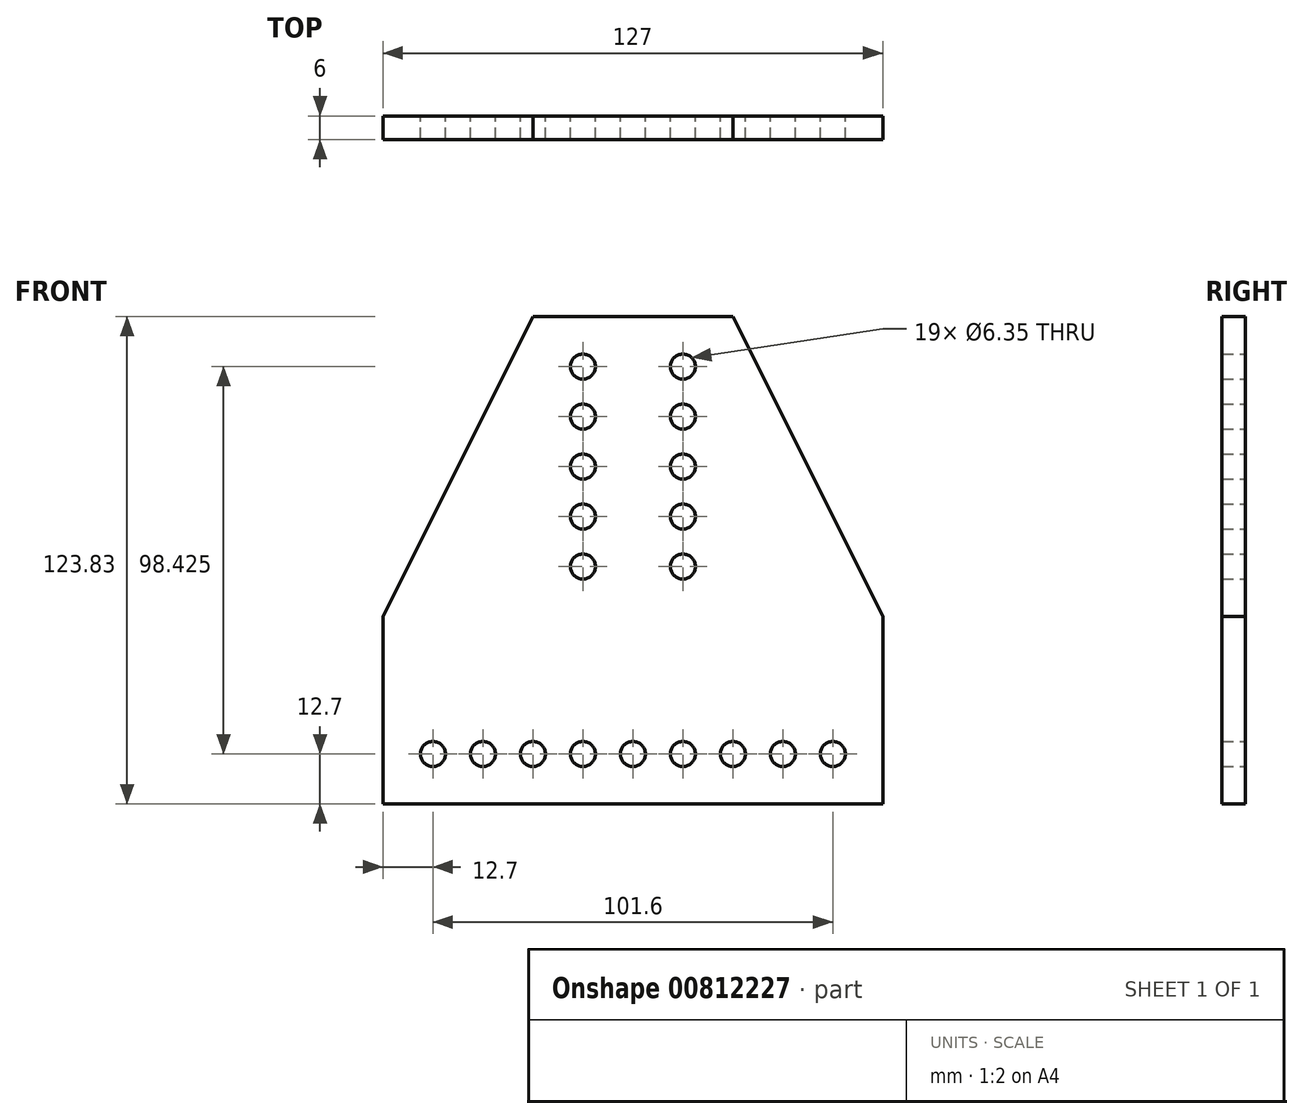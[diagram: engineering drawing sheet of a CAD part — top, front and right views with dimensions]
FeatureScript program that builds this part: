
annotation { "Feature Type Name" : "Feature", "Feature Type Description" : "" }
export const myFeature = defineFeature(function(context is Context, id is Id, definition is map)
    precondition{}
    {
        {
            var Q0;
            Q0=qCreatedBy(makeId("Front.planeOp"),FACE);
            var sketch = newSketch(context, id + "F0", { "sketchPlane" : qUnion([Q0])});
            skLineSegment(sketch, "E0.bottom", {"start": v(-63.5, 0) * mm, "end": v(63.5, 0) * mm, "construction": true});
            skLineSegment(sketch, "E0.top", {"start": v(-63.5, 25.4) * mm, "end": v(63.5, 25.4) * mm, "construction": true});
            skLineSegment(sketch, "E0.left", {"start": v(-63.5, 0) * mm, "end": v(-63.5, 25.4) * mm, "construction": true});
            skLineSegment(sketch, "E0.right", {"start": v(63.5, 0) * mm, "end": v(63.5, 25.4) * mm, "construction": true});
            skPoint(sketch, "E0.middle", {"position": v(0, 12.7) * mm});
            skLineSegment(sketch, "E1", {"start": v(-63.5, 25.4) * mm, "end": v(-63.5, 47.63) * mm, "construction": true});
            skLineSegment(sketch, "E2", {"start": v(-63.5, 47.63) * mm, "end": v(63.5, 47.63) * mm, "construction": true});
            skLineSegment(sketch, "E3", {"start": v(63.5, 47.63) * mm, "end": v(63.5, 25.4) * mm, "construction": true});
            skLineSegment(sketch, "E4", {"start": v(-63.5, 47.63) * mm, "end": v(-63.5, 0) * mm});
            skLineSegment(sketch, "E5", {"start": v(-63.5, 0) * mm, "end": v(63.5, 0) * mm});
            skLineSegment(sketch, "E6", {"start": v(63.5, 0) * mm, "end": v(63.5, 47.63) * mm});
            skLineSegment(sketch, "E7", {"start": v(63.5, 47.62) * mm, "end": v(25.4, 123.83) * mm});
            skLineSegment(sketch, "E8", {"start": v(25.4, 123.83) * mm, "end": v(-25.4, 123.83) * mm});
            skLineSegment(sketch, "E9", {"start": v(-25.4, 123.83) * mm, "end": v(-63.5, 47.62) * mm});
            skLineSegment(sketch, "E10", {"start": v(0, 123.83) * mm, "end": v(0, 12.7) * mm, "construction": true});
            skCircle(sketch, "E11", {"center": v(-50.8, 12.7) * mm, "radius": 3.18 * mm});
            skCircle(sketch, "E12.1.0.0", {"center": v(-38.1, 12.7) * mm, "radius": 3.18 * mm});
            skCircle(sketch, "E12.2.0.0", {"center": v(-25.4, 12.7) * mm, "radius": 3.18 * mm});
            skCircle(sketch, "E12.3.0.0", {"center": v(-12.7, 12.7) * mm, "radius": 3.18 * mm});
            skCircle(sketch, "E12.4.0.0", {"center": v(0, 12.7) * mm, "radius": 3.18 * mm});
            skCircle(sketch, "E12.5.0.0", {"center": v(12.7, 12.7) * mm, "radius": 3.18 * mm});
            skCircle(sketch, "E12.6.0.0", {"center": v(25.4, 12.7) * mm, "radius": 3.18 * mm});
            skCircle(sketch, "E12.7.0.0", {"center": v(38.1, 12.7) * mm, "radius": 3.18 * mm});
            skCircle(sketch, "E12.8.0.0", {"center": v(50.8, 12.7) * mm, "radius": 3.18 * mm});
            skLineSegment(sketch, "E12.direction1", {"start": v(-50.8, 12.7) * mm, "end": v(-38.1, 12.7) * mm, "construction": true});
            skCircle(sketch, "E13", {"center": v(-12.7, 111.13) * mm, "radius": 3.18 * mm});
            skCircle(sketch, "E14.0.1.0", {"center": v(-12.7, 98.43) * mm, "radius": 3.18 * mm});
            skCircle(sketch, "E14.0.2.0", {"center": v(-12.7, 85.73) * mm, "radius": 3.18 * mm});
            skCircle(sketch, "E14.1.0.0", {"center": v(12.7, 111.13) * mm, "radius": 3.18 * mm});
            skCircle(sketch, "E14.1.1.0", {"center": v(12.7, 98.43) * mm, "radius": 3.18 * mm});
            skCircle(sketch, "E14.1.2.0", {"center": v(12.7, 85.73) * mm, "radius": 3.18 * mm});
            skLineSegment(sketch, "E14.direction1", {"start": v(-12.7, 111.13) * mm, "end": v(12.7, 111.13) * mm, "construction": true});
            skLineSegment(sketch, "E14.direction2", {"start": v(-12.7, 111.13) * mm, "end": v(-12.7, 98.43) * mm, "construction": true});
            skCircle(sketch, "E15.0.0.3", {"center": v(-12.7, 73.03) * mm, "radius": 3.18 * mm});
            skCircle(sketch, "E15.0.0.4", {"center": v(-12.7, 60.33) * mm, "radius": 3.18 * mm});
            skCircle(sketch, "E15.0.1.3", {"center": v(12.7, 73.03) * mm, "radius": 3.18 * mm});
            skCircle(sketch, "E15.0.1.4", {"center": v(12.7, 60.33) * mm, "radius": 3.18 * mm});
            skSolve(sketch);
        }
        {
            var Q0;
            Q0 = qSketchRegion(id + "F0", true);
            extrude(context, id + "F1", {"entities" : qUnion([Q0]), "depth" : 6 * mm, "offsetDistance" : 25.4 * mm});
        }
    });
